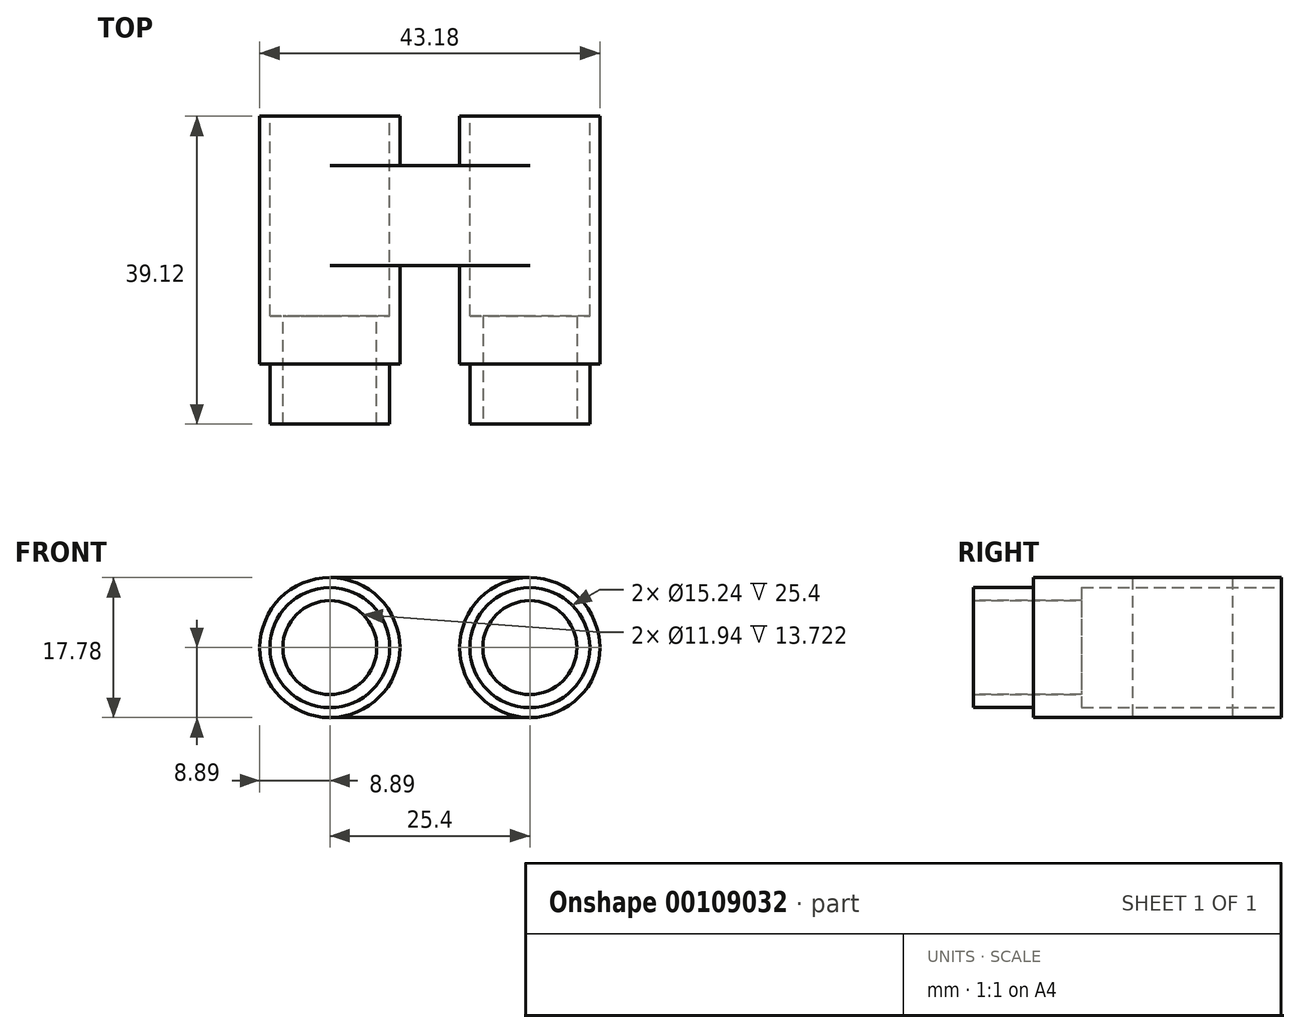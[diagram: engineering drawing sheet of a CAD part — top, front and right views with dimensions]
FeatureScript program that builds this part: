
annotation { "Feature Type Name" : "Feature", "Feature Type Description" : "" }
export const myFeature = defineFeature(function(context is Context, id is Id, definition is map)
    precondition{}
    {
        {
            var Q0;
            Q0=qCreatedBy(makeId("Top.planeOp"),FACE);
            var sketch = newSketch(context, id + "F0", { "sketchPlane" : qUnion([Q0])});
            skLineSegment(sketch, "E0", {"start": v(0, 0) * mm, "end": v(25.4, 0) * mm});
            skLineSegment(sketch, "E1", {"start": v(0, 0) * mm, "end": v(0, 68.94) * mm});
            skLineSegment(sketch, "E2", {"start": v(25.4, 0) * mm, "end": v(25.4, 68.94) * mm});
            skArc(sketch, "E3", {"start": v(0, 68.94) * mm, "mid": v(12.7, 81.64) * mm, "end": v(25.4, 68.94) * mm});
            skLineSegment(sketch, "E4", {"start": v(12.7, 81.64) * mm, "end": v(12.7, 39.12) * mm});
            skLineSegment(sketch, "E5", {"start": v(12.7, 39.12) * mm, "end": v(39.42, 39.12) * mm});
            skLineSegment(sketch, "E6", {"start": v(39.42, 39.12) * mm, "end": v(39.42, 94.54) * mm});
            skLineSegment(sketch, "E7", {"start": v(39.42, 94.54) * mm, "end": v(-11.2, 94.54) * mm});
            skLineSegment(sketch, "E8", {"start": v(-11.2, 94.54) * mm, "end": v(-11.2, 39.12) * mm});
            skLineSegment(sketch, "E9", {"start": v(-11.2, 39.12) * mm, "end": v(12.7, 39.12) * mm});
            skLineSegment(sketch, "E10", {"start": v(0, 32.87) * mm, "end": v(25.4, 32.87) * mm});
            skPoint(sketch, "E10.endSnap0", {"position": v(25.4, 34.47) * mm});
            skLineSegment(sketch, "E11", {"start": v(0, 20.17) * mm, "end": v(25.4, 20.17) * mm});
            skSolve(sketch);
        }
        {
            var Q0;
            Q0=qCreatedBy(makeId("Front.planeOp"),FACE);
            var sketch = newSketch(context, id + "F1", { "sketchPlane" : qUnion([Q0])});
            skCircle(sketch, "E12", {"center": v(0, 0) * mm, "radius": 5.97 * mm});
            skCircle(sketch, "E13", {"center": v(0, 0) * mm, "radius": 8.9 * mm});
            skSolve(sketch);
        }
        {
            var Q0;
            Q0=makeQuery(id+"F1.imprint","IMPRINT",FACE,{"disambiguationData":[TD([[makeQuery(id+"F1.imprint","IMPRINT",EDGE,{"derivedFrom":sQuery(id+"F1.wireOp",EDGE,"E12")}),-1.0]])]});
            var Q1;
            Q1=sQuery(id+"F0.wireOp",EDGE,"E1");
            var Q2;
            Q2=sQuery(id+"F0.wireOp",EDGE,"E3");
            var Q3;
            Q3=sQuery(id+"F0.wireOp",EDGE,"E2");
            sweep(context, id + "F2", {"profiles" : qUnion([Q0]), "path" : qUnion([Q1, Q2, Q3])});
        }
        {
            var Q0;
            Q0=makeQuery(id+"F2.opSweep","CAP_FACE",FACE,{"disambiguationData":[OSD([sQuery(id+"F0.wireOp",VERTEX,"E1.start"),sQuery(id+"F1.wireOp",EDGE,"E12"),sQuery(id+"F1.wireOp",EDGE,"E13")])],"isStart":true});
            var sketch = newSketch(context, id + "F3", { "sketchPlane" : qUnion([Q0])});
            skCircle(sketch, "E14", {"center": v(0, 0) * mm, "radius": 7.62 * mm});
            skCircle(sketch, "E15", {"center": v(25.4, 0) * mm, "radius": 7.62 * mm});
            skLineSegment(sketch, "E16", {"start": v(0, 0) * mm, "end": v(25.4, 0) * mm});
            skCircle(sketch, "E17", {"center": v(25.4, 0) * mm, "radius": 8.9 * mm});
            skSolve(sketch);
        }
        {
            var Q0;
            Q0=makeQuery(id+"F3.imprint","IMPRINT",FACE,{"disambiguationData":[TD([[makeQuery(id+"F3.imprint","IMPRINT",EDGE,{"derivedFrom":sQuery(id+"F3.wireOp",EDGE,"E14")}),-1.0]])]});
            var Q1;
            Q1=makeQuery(id+"F3.imprint","IMPRINT",FACE,{"disambiguationData":[TD([[makeQuery(id+"F3.imprint","IMPRINT",EDGE,{"derivedFrom":sQuery(id+"F3.wireOp",EDGE,"E15")}),-1.0]])]});
            extrude(context, id + "F4", {"entities" : qUnion([Q0, Q1]), "operationType" : NewBodyOperationType.REMOVE, "oppositeDirection" : true, "depth" : 7.62 * mm});
        }
        {
            var Q0;
            {var subQ11=sQuery(id+"F0.wireOp",EDGE,"E6");Q0=makeQuery(id+"F0.imprint","IMPRINT",FACE,{"disambiguationData":[TD([[makeQuery(id+"F0.imprint","IMPRINT",EDGE,{"derivedFrom":subQ11}),1.0]])]});}
            var Q1;
            {var subQ5=sQuery(id+"F0.wireOp",EDGE,"E4");Q1=makeQuery(id+"F0.imprint","IMPRINT",FACE,{"disambiguationData":[TD([[makeQuery(id+"F0.imprint","IMPRINT",EDGE,{"derivedFrom":subQ5}),-1.0]])]});}
            var Q2;
            {var subQ5=sQuery(id+"F0.wireOp",EDGE,"E4");Q2=makeQuery(id+"F0.imprint","IMPRINT",FACE,{"disambiguationData":[TD([[makeQuery(id+"F0.imprint","IMPRINT",EDGE,{"derivedFrom":subQ5}),1.0]])]});}
            extrude(context, id + "F5", {"entities" : qUnion([Q0, Q1, Q2]), "operationType" : NewBodyOperationType.REMOVE, "depth" : 25.4 * mm, "hasSecondDirection" : true, "secondDirectionOppositeDirection" : true, "secondDirectionDepth" : 25.4 * mm});
        }
        {
            var Q0;
            Q0=makeQuery(id+"F5.boolean.opBoolean","COPY",FACE,{"disambiguationData":[OD(0.0)],"derivedFrom":makeQuery(id+"F5.opExtrude","SWEPT_FACE",FACE,{"disambiguationData":[OSD([sQuery(id+"F0.wireOp",EDGE,"E5"),sQuery(id+"F0.wireOp",EDGE,"E9")])]})});
            var sketch = newSketch(context, id + "F6", { "sketchPlane" : qUnion([Q0])});
            skCircle(sketch, "E18", {"center": v(0, 0) * mm, "radius": 7.62 * mm});
            skSolve(sketch);
        }
        {
            var Q0;
            Q0=makeQuery(id+"F5.boolean.opBoolean","COPY",FACE,{"disambiguationData":[OD(1.0)],"derivedFrom":makeQuery(id+"F5.opExtrude","SWEPT_FACE",FACE,{"disambiguationData":[OSD([sQuery(id+"F0.wireOp",EDGE,"E5"),sQuery(id+"F0.wireOp",EDGE,"E9")])]})});
            var sketch = newSketch(context, id + "F7", { "sketchPlane" : qUnion([Q0])});
            skCircle(sketch, "E19", {"center": v(-25.4, 0) * mm, "radius": 7.62 * mm});
            skSolve(sketch);
        }
        {
            var Q0;
            Q0=makeQuery(id+"F6.imprint","IMPRINT",FACE,{"disambiguationData":[TD([[makeQuery(id+"F6.imprint","IMPRINT",EDGE,{"derivedFrom":sQuery(id+"F6.wireOp",EDGE,"E18")}),1.0]])]});
            var Q1;
            Q1=makeQuery(id+"F7.imprint","IMPRINT",FACE,{"disambiguationData":[TD([[makeQuery(id+"F7.imprint","IMPRINT",EDGE,{"derivedFrom":sQuery(id+"F7.wireOp",EDGE,"E19")}),1.0]])]});
            extrude(context, id + "F8", {"entities" : qUnion([Q0, Q1]), "operationType" : NewBodyOperationType.REMOVE, "oppositeDirection" : true, "depth" : 25.4 * mm});
        }
        {
            var Q0;
            {var subQ0=sQuery(id+"F0.wireOp",EDGE,"E10");Q0=makeQuery(id+"F0.imprint","IMPRINT",FACE,{"disambiguationData":[TD([[makeQuery(id+"F0.imprint","IMPRINT",EDGE,{"derivedFrom":subQ0}),-1.0]])]});}
            extrude(context, id + "F9", {"entities" : qUnion([Q0]), "operationType" : NewBodyOperationType.ADD, "depth" : 8.9 * mm, "hasSecondDirection" : true, "secondDirectionOppositeDirection" : true, "secondDirectionDepth" : 8.9 * mm});
        }
        {
            var Q0;
            Q0 = qSketchRegion(id + "F7", true);
            var Q1;
            Q1 = qSketchRegion(id + "F6", true);
            extrude(context, id + "F10", {"entities" : qUnion([Q0, Q1]), "operationType" : NewBodyOperationType.REMOVE, "oppositeDirection" : true, "depth" : 25.4 * mm});
        }
    });
